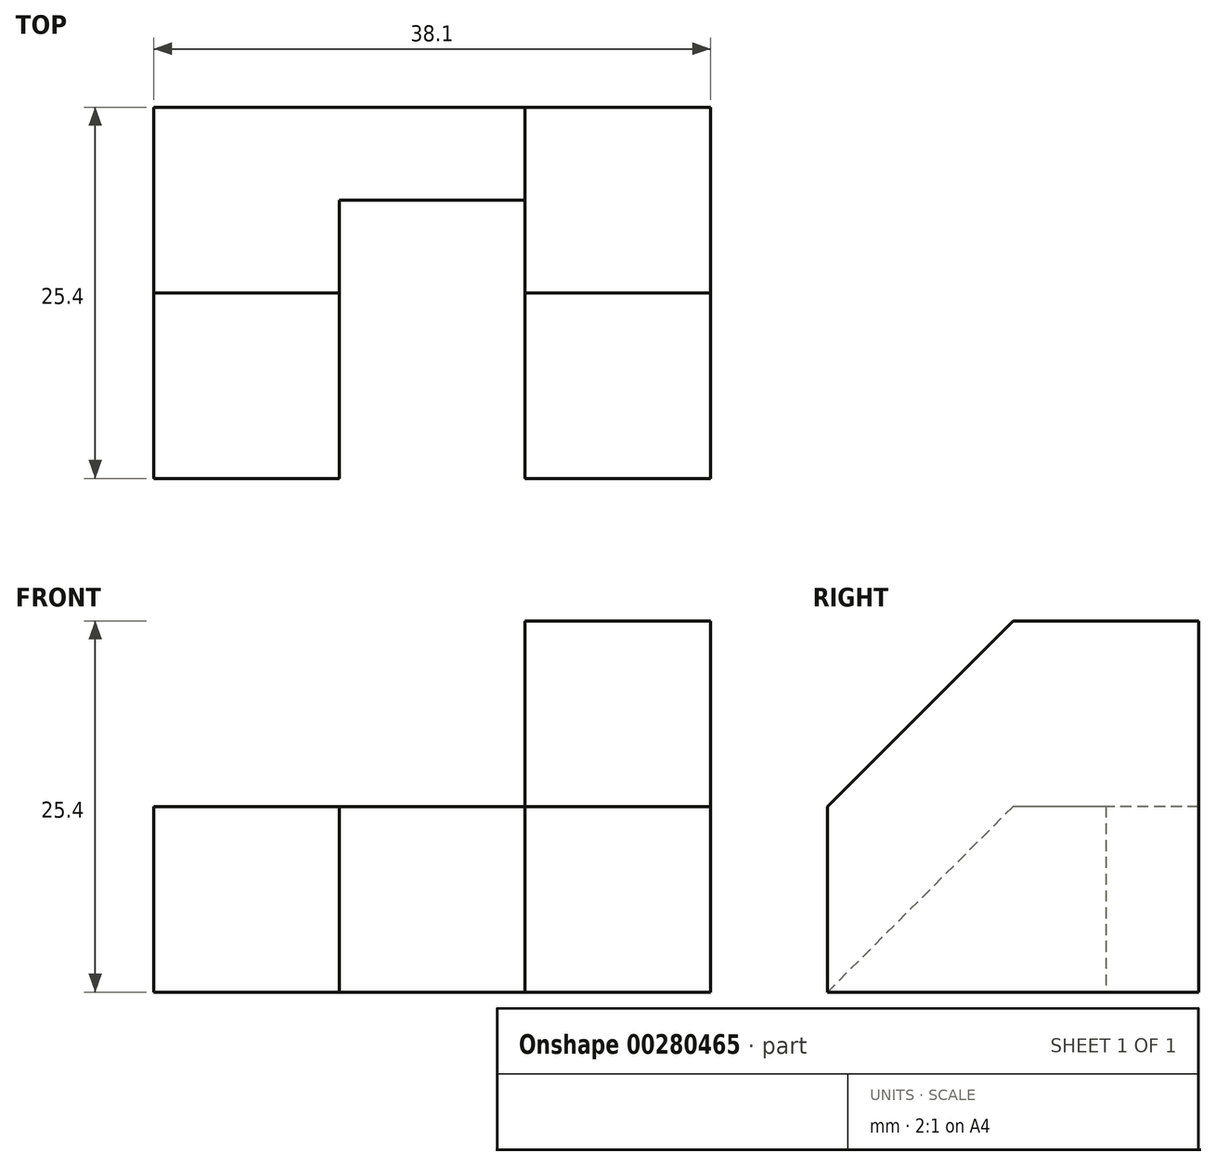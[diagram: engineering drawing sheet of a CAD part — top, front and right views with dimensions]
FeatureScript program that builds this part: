
annotation { "Feature Type Name" : "Feature", "Feature Type Description" : "" }
export const myFeature = defineFeature(function(context is Context, id is Id, definition is map)
    precondition{}
    {
        {
            var Q0;
            Q0=qCreatedBy(makeId("Right.planeOp"),FACE);
            var sketch = newSketch(context, id + "F0", { "sketchPlane" : qUnion([Q0])});
            skLineSegment(sketch, "E0", {"start": v(0, 0) * mm, "end": v(0, 12.7) * mm});
            skLineSegment(sketch, "E1", {"start": v(0, 12.7) * mm, "end": v(12.7, 25.4) * mm});
            skLineSegment(sketch, "E2", {"start": v(12.7, 25.4) * mm, "end": v(25.4, 25.4) * mm});
            skLineSegment(sketch, "E3", {"start": v(25.4, 25.4) * mm, "end": v(25.4, 0) * mm});
            skLineSegment(sketch, "E4", {"start": v(25.4, 0) * mm, "end": v(0, 0) * mm});
            skSolve(sketch);
        }
        {
            var Q0;
            Q0=makeQuery(id+"F0.imprint","IMPRINT",FACE,{"disambiguationData":[TD([[makeQuery(id+"F0.imprint","IMPRINT",EDGE,{"derivedFrom":sQuery(id+"F0.wireOp",EDGE,"E0")}),-1.0]])]});
            extrude(context, id + "F1", {"entities" : qUnion([Q0]), "depth" : 12.7 * mm});
        }
        {
            var Q0;
            Q0=qCreatedBy(makeId("Right.planeOp"),FACE);
            var sketch = newSketch(context, id + "F2", { "sketchPlane" : qUnion([Q0])});
            skLineSegment(sketch, "E5", {"start": v(0, 0) * mm, "end": v(25.4, 0) * mm});
            skLineSegment(sketch, "E6", {"start": v(25.4, 0) * mm, "end": v(25.4, 12.7) * mm});
            skLineSegment(sketch, "E7", {"start": v(25.4, 12.7) * mm, "end": v(12.7, 12.7) * mm});
            skLineSegment(sketch, "E8", {"start": v(12.7, 12.7) * mm, "end": v(0, 0) * mm});
            skSolve(sketch);
        }
        {
            var Q0;
            Q0 = qSketchRegion(id + "F2", true);
            extrude(context, id + "F3", {"entities" : qUnion([Q0]), "operationType" : NewBodyOperationType.ADD, "oppositeDirection" : true, "depth" : 25.4 * mm});
        }
        {
            var Q0;
            Q0=qCreatedBy(makeId("Top.planeOp"),FACE);
            var sketch = newSketch(context, id + "F4", { "sketchPlane" : qUnion([Q0])});
            skLineSegment(sketch, "E9.bottom", {"start": v(0, 0) * mm, "end": v(-12.7, 0) * mm});
            skLineSegment(sketch, "E9.top", {"start": v(0, 19.05) * mm, "end": v(-12.7, 19.05) * mm});
            skLineSegment(sketch, "E9.left", {"start": v(0, 0) * mm, "end": v(0, 19.05) * mm});
            skLineSegment(sketch, "E9.right", {"start": v(-12.7, 0) * mm, "end": v(-12.7, 19.05) * mm});
            skSolve(sketch);
        }
        {
            var Q0;
            Q0 = qSketchRegion(id + "F4", true);
            extrude(context, id + "F5", {"entities" : qUnion([Q0]), "operationType" : NewBodyOperationType.REMOVE, "endBound" : BoundingType.THROUGH_ALL, "depth" : 25.4 * mm});
        }
    });
